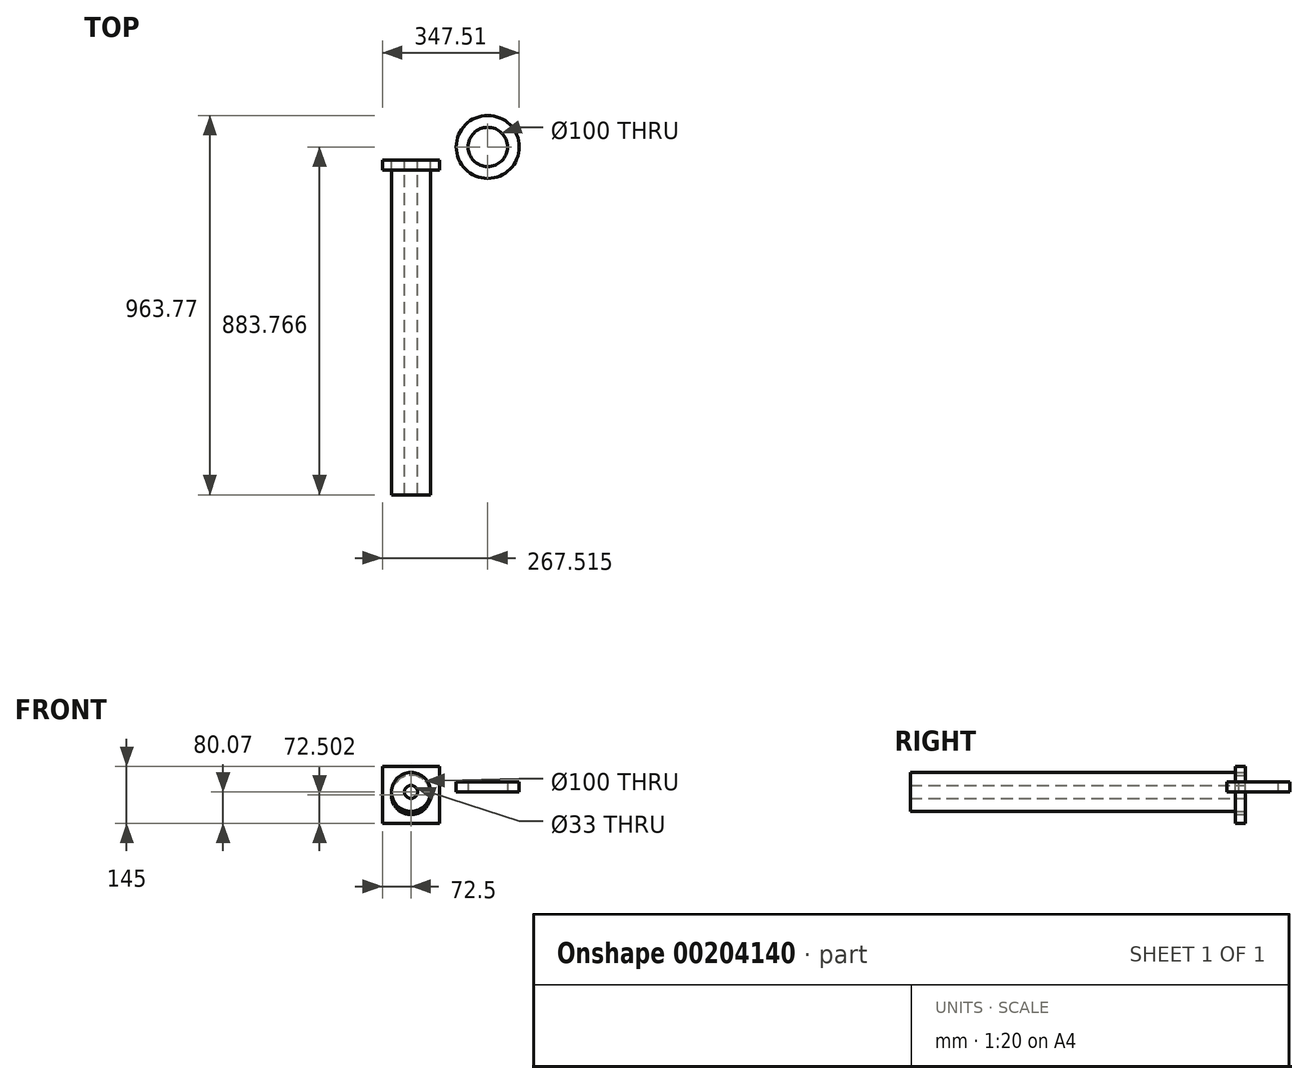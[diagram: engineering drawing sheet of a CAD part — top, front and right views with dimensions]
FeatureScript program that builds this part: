
annotation { "Feature Type Name" : "Feature", "Feature Type Description" : "" }
export const myFeature = defineFeature(function(context is Context, id is Id, definition is map)
    precondition{}
    {
        {
            var Q0;
            Q0=qCreatedBy(makeId("Front.planeOp"),FACE);
            var sketch = newSketch(context, id + "F0", { "sketchPlane" : qUnion([Q0])});
            skCircle(sketch, "E0", {"center": v(0, 0) * mm, "radius": 16.5 * mm});
            skCircle(sketch, "E1", {"center": v(0, 0) * mm, "radius": 49.5 * mm});
            skSolve(sketch);
        }
        {
            var Q0;
            Q0 = qSketchRegion(id + "F0", true);
            extrude(context, id + "F1", {"entities" : qUnion([Q0]), "depth" : 850.9 * mm});
        }
        {
            var Q0;
            Q0=qCreatedBy(makeId("Top.planeOp"),FACE);
            var sketch = newSketch(context, id + "F2", { "sketchPlane" : qUnion([Q0])});
            skCircle(sketch, "E2", {"center": v(195.01, 32.87) * mm, "radius": 50 * mm});
            skCircle(sketch, "E3", {"center": v(195.01, 32.87) * mm, "radius": 80 * mm});
            skSolve(sketch);
        }
        {
            var Q0;
            Q0=qCreatedBy(makeId("Front.planeOp"),FACE);
            var sketch = newSketch(context, id + "F3", { "sketchPlane" : qUnion([Q0])});
            skLineSegment(sketch, "E4.bottom", {"start": v(72.5, -80.07) * mm, "end": v(-72.5, -80.07) * mm});
            skLineSegment(sketch, "E4.top", {"start": v(72.5, 64.93) * mm, "end": v(-72.5, 64.93) * mm});
            skLineSegment(sketch, "E4.left", {"start": v(72.5, -80.07) * mm, "end": v(72.5, 64.93) * mm});
            skLineSegment(sketch, "E4.right", {"start": v(-72.5, -80.07) * mm, "end": v(-72.5, 64.93) * mm});
            skPoint(sketch, "E4.middle", {"position": v(0, -7.57) * mm});
            skCircle(sketch, "E5", {"center": v(0, -7.57) * mm, "radius": 50 * mm});
            skSolve(sketch);
        }
        {
            var Q0;
            Q0=makeQuery(id+"F2.imprint","IMPRINT",FACE,{"disambiguationData":[TD([[makeQuery(id+"F2.imprint","IMPRINT",EDGE,{"derivedFrom":sQuery(id+"F2.wireOp",EDGE,"E2")}),-1.0]])]});
            extrude(context, id + "F4", {"entities" : qUnion([Q0]), "depth" : 25.4 * mm});
        }
        {
            var Q0;
            Q0=makeQuery(id+"F3.imprint","IMPRINT",FACE,{"disambiguationData":[TD([[makeQuery(id+"F3.imprint","IMPRINT",EDGE,{"derivedFrom":sQuery(id+"F3.wireOp",EDGE,"E4.bottom")}),-1.0]])]});
            extrude(context, id + "F5", {"entities" : qUnion([Q0]), "depth" : 25.4 * mm});
        }
    });
